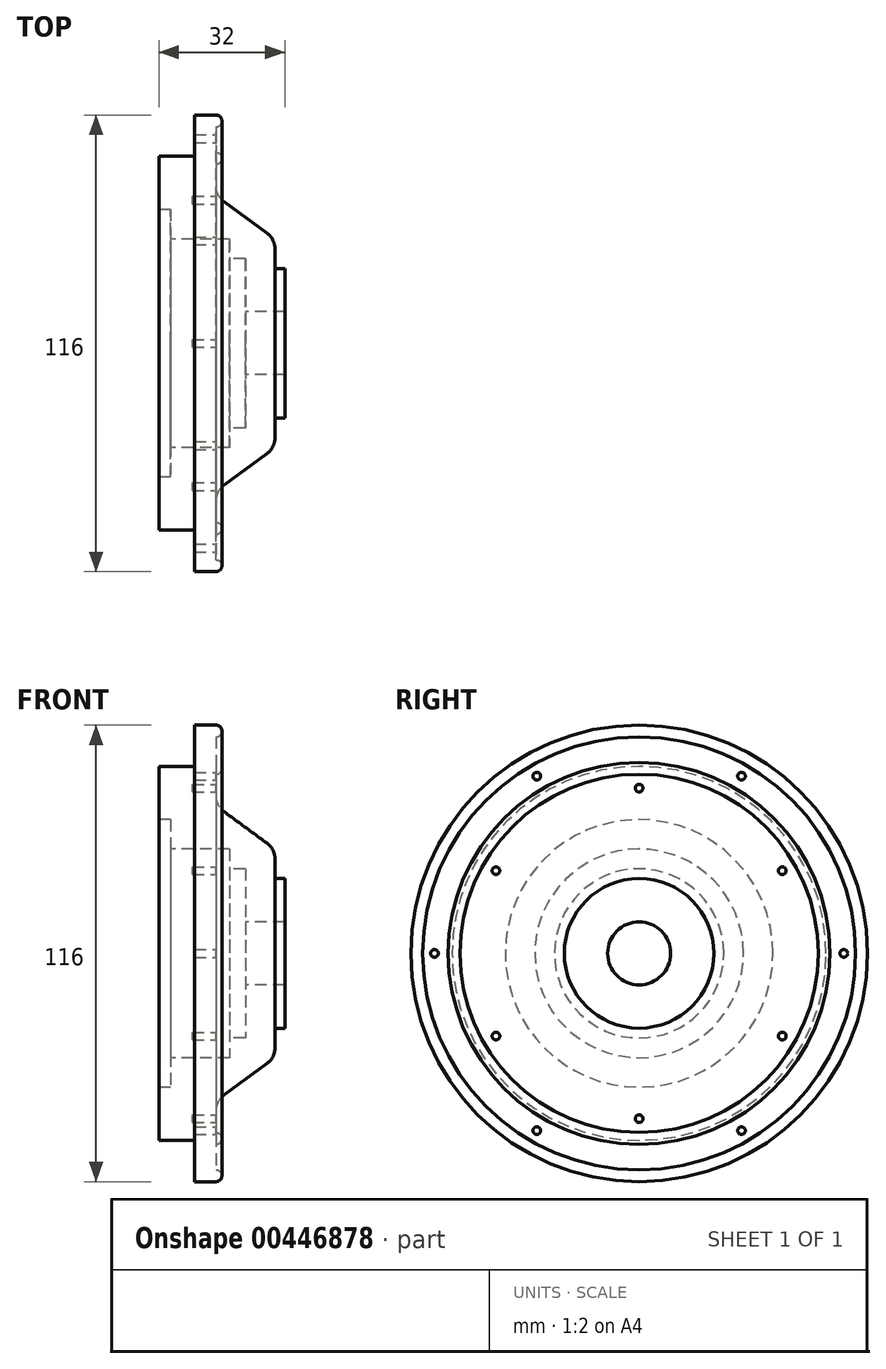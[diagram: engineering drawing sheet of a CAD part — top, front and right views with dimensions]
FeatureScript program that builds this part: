
annotation { "Feature Type Name" : "Feature", "Feature Type Description" : "" }
export const myFeature = defineFeature(function(context is Context, id is Id, definition is map)
    precondition{}
    {
        {
            var Q0;
            Q0=qCreatedBy(makeId("Top.planeOp"),FACE);
            var sketch = newSketch(context, id + "F0", { "sketchPlane" : qUnion([Q0])});
            skLineSegment(sketch, "E0", {"start": v(0, 0) * mm, "end": v(0, 34) * mm, "construction": true});
            skLineSegment(sketch, "E1", {"start": v(0, 34) * mm, "end": v(3, 34) * mm});
            skLineSegment(sketch, "E2", {"start": v(3, 34) * mm, "end": v(3, 26.5) * mm});
            skLineSegment(sketch, "E3", {"start": v(0, 34) * mm, "end": v(0, 47.5) * mm});
            skLineSegment(sketch, "E4", {"start": v(0, 47.5) * mm, "end": v(9, 47.5) * mm});
            skLineSegment(sketch, "E5", {"start": v(9, 47.5) * mm, "end": v(9, 58) * mm});
            skLineSegment(sketch, "E6", {"start": v(9, 58) * mm, "end": v(14.5, 58) * mm});
            skLineSegment(sketch, "E7", {"start": v(16, 56.5) * mm, "end": v(16, 56.5) * mm});
            skLineSegment(sketch, "E8", {"start": v(14.5, 55) * mm, "end": v(14.5, 55) * mm});
            skLineSegment(sketch, "E9", {"start": v(14.5, 55) * mm, "end": v(14.5, 48.5) * mm});
            skLineSegment(sketch, "E10", {"start": v(14.5, 48.5) * mm, "end": v(14.5, 48.5) * mm});
            skLineSegment(sketch, "E11", {"start": v(0, 0) * mm, "end": v(29.5, 0) * mm, "construction": true});
            skLineSegment(sketch, "E12", {"start": v(29.5, 0) * mm, "end": v(29.5, 26.5) * mm, "construction": true});
            skLineSegment(sketch, "E13", {"start": v(29.5, 23.97) * mm, "end": v(29.5, 19) * mm});
            skLineSegment(sketch, "E14", {"start": v(29.5, 19) * mm, "end": v(32, 19) * mm});
            skLineSegment(sketch, "E15", {"start": v(32, 19) * mm, "end": v(32, 8) * mm});
            skLineSegment(sketch, "E16", {"start": v(3, 26.5) * mm, "end": v(18, 26.5) * mm});
            skLineSegment(sketch, "E17", {"start": v(18, 26.5) * mm, "end": v(18, 21.5) * mm});
            skLineSegment(sketch, "E18", {"start": v(18, 21.5) * mm, "end": v(22, 21.5) * mm});
            skLineSegment(sketch, "E19", {"start": v(22, 21.5) * mm, "end": v(22, 8) * mm});
            skLineSegment(sketch, "E20", {"start": v(22, 8) * mm, "end": v(32, 8) * mm});
            skPoint(sketch, "E21.visualSharp", {"position": v(16, 58) * mm});
            skArc(sketch, "E21.filletArc", {"start": v(16, 56.5) * mm, "mid": v(15.56, 57.56) * mm, "end": v(14.5, 58) * mm});
            skPoint(sketch, "E22.visualSharp", {"position": v(16, 55) * mm});
            skArc(sketch, "E22.filletArc", {"start": v(14.5, 55) * mm, "mid": v(15.56, 55.44) * mm, "end": v(16, 56.5) * mm});
            skLineSegment(sketch, "E23", {"start": v(16, 47) * mm, "end": v(16, 47) * mm});
            skLineSegment(sketch, "E24", {"start": v(14.5, 45.5) * mm, "end": v(14.5, 45.5) * mm});
            skPoint(sketch, "E25.visualSharp", {"position": v(16, 48.5) * mm});
            skArc(sketch, "E25.filletArc", {"start": v(16, 47) * mm, "mid": v(15.56, 48.06) * mm, "end": v(14.5, 48.5) * mm});
            skPoint(sketch, "E26.visualSharp", {"position": v(16, 45.5) * mm});
            skArc(sketch, "E26.filletArc", {"start": v(14.5, 45.5) * mm, "mid": v(15.56, 45.94) * mm, "end": v(16, 47) * mm});
            skLineSegment(sketch, "E27", {"start": v(14.5, 45.5) * mm, "end": v(14.5, 40.03) * mm});
            skLineSegment(sketch, "E28", {"start": v(16.54, 36) * mm, "end": v(27.46, 28) * mm});
            skPoint(sketch, "E29.visualSharp", {"position": v(14.5, 37.5) * mm});
            skArc(sketch, "E29.filletArc", {"start": v(14.5, 40.03) * mm, "mid": v(15.04, 37.77) * mm, "end": v(16.54, 36) * mm});
            skPoint(sketch, "E30.visualSharp", {"position": v(29.5, 26.5) * mm});
            skArc(sketch, "E30.filletArc", {"start": v(29.5, 23.97) * mm, "mid": v(28.96, 26.23) * mm, "end": v(27.46, 28) * mm});
            skLineSegment(sketch, "E31", {"start": v(0, 0) * mm, "end": v(0, 42) * mm, "construction": true});
            skLineSegment(sketch, "E32", {"start": v(0, 42) * mm, "end": v(38.78, 42) * mm, "construction": true});
            skLineSegment(sketch, "E33", {"start": v(38.78, 42) * mm, "end": v(38.78, 52) * mm, "construction": true});
            skLineSegment(sketch, "E34", {"start": v(38.78, 52) * mm, "end": v(-20.8, 52) * mm, "construction": true});
            skSolve(sketch);
        }
        {
            var Q0;
            Q0 = qSketchRegion(id + "F0", true);
            var Q1;
            Q1=sQuery(id+"F0.wireOp",EDGE,"E11");
            revolve(context, id + "F1", {"entities" : qUnion([Q0]), "axis" : qUnion([Q1]), "revolveType" : RevolveType.FULL});
        }
        {
            var Q0;
            Q0=makeQuery(id+"F1.opRevolve","SWEPT_FACE",FACE,{"disambiguationData":[OSD([sQuery(id+"F0.wireOp",EDGE,"E27")])]});
            cPlane(context, id + "F2", {"entities" : qUnion([Q0]), "cplaneType" : CPlaneType.OFFSET, "offset" : 0 * mm, "width" : 150 * mm, "height" : 150 * mm});
        }
        {
            var Q0;
            Q0=qCreatedBy(id+"F2.planeOp",FACE);
            var sketch = newSketch(context, id + "F3", { "sketchPlane" : qUnion([Q0])});
            skLineSegment(sketch, "E35", {"start": v(0, 0) * mm, "end": v(0, -42) * mm, "construction": true});
            skCircle(sketch, "E36", {"center": v(0, -42) * mm, "radius": 0.98 * mm});
            skCircle(sketch, "E37.1.0", {"center": v(36.37, -21) * mm, "radius": 0.98 * mm});
            skCircle(sketch, "E37.2.0", {"center": v(36.37, 21) * mm, "radius": 0.98 * mm});
            skCircle(sketch, "E37.3.0", {"center": v(0, 42) * mm, "radius": 0.98 * mm});
            skCircle(sketch, "E37.4.0", {"center": v(-36.37, 21) * mm, "radius": 0.98 * mm});
            skCircle(sketch, "E37.5.0", {"center": v(-36.37, -21) * mm, "radius": 0.98 * mm});
            skPoint(sketch, "E37.center", {"position": v(0, 0) * mm});
            skLineSegment(sketch, "E38", {"start": v(0, 0) * mm, "end": v(52, 0) * mm, "construction": true});
            skCircle(sketch, "E39", {"center": v(52, 0) * mm, "radius": 0.98 * mm});
            skCircle(sketch, "E40.1.0", {"center": v(26, 45.03) * mm, "radius": 0.98 * mm});
            skCircle(sketch, "E40.2.0", {"center": v(-26, 45.03) * mm, "radius": 0.98 * mm});
            skCircle(sketch, "E40.3.0", {"center": v(-52, 0) * mm, "radius": 0.98 * mm});
            skCircle(sketch, "E40.4.0", {"center": v(-26, -45.03) * mm, "radius": 0.98 * mm});
            skCircle(sketch, "E40.5.0", {"center": v(26, -45.03) * mm, "radius": 0.98 * mm});
            skSolve(sketch);
        }
        {
            var Q0;
            Q0 = qSketchRegion(id + "F3", true);
            extrude(context, id + "F4", {"entities" : qUnion([Q0]), "operationType" : NewBodyOperationType.REMOVE, "oppositeDirection" : true, "depth" : 6 * mm, "offsetDistance" : 25 * mm});
        }
    });
